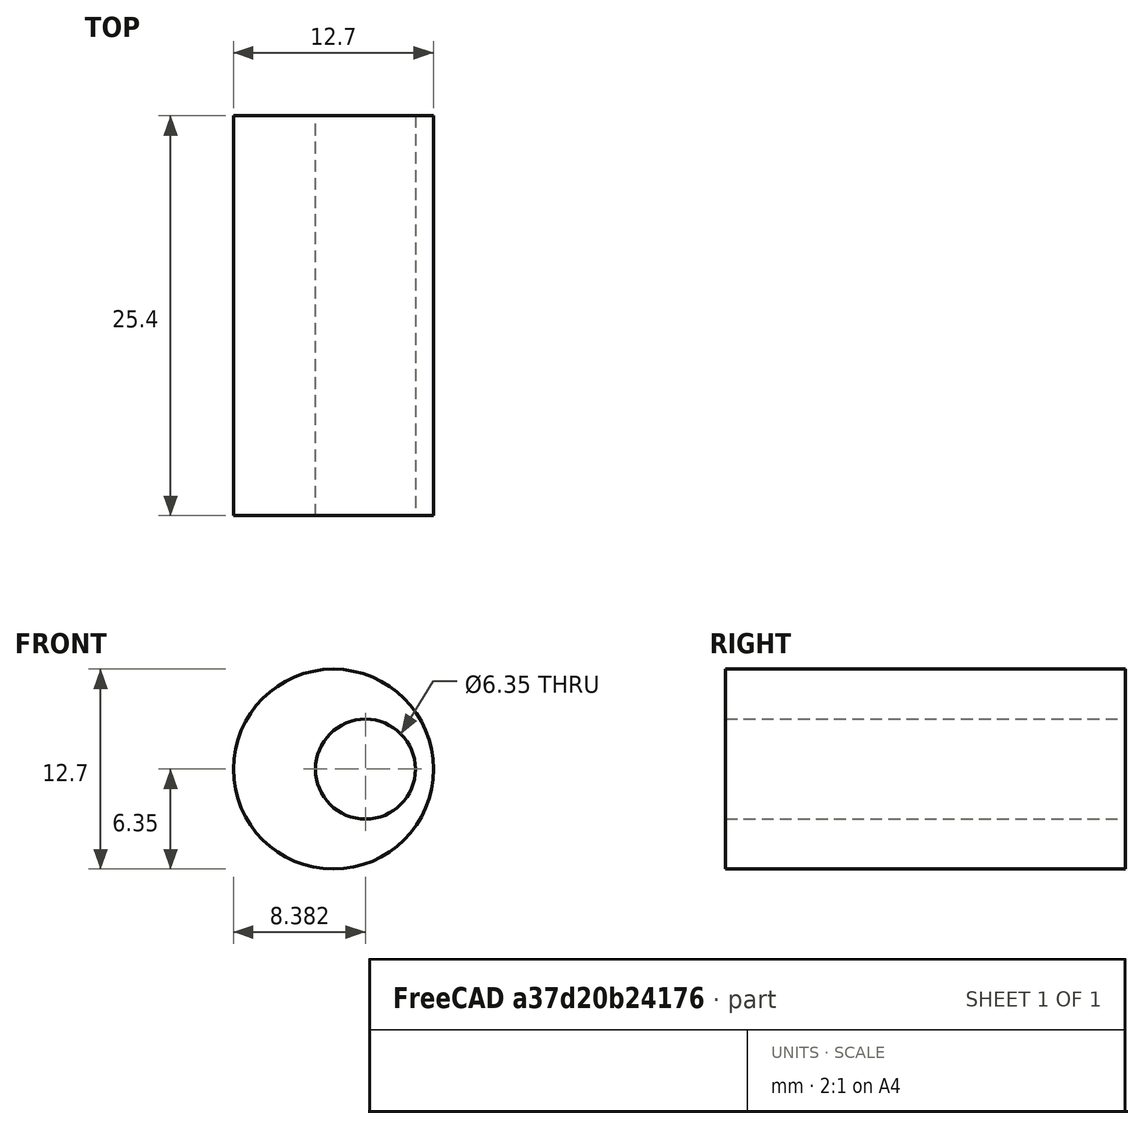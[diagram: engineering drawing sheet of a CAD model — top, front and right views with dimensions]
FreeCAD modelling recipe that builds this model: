
FCSTD DOCUMENT  (FreeCAD 0.21R31527 (Git))
Label: TempCam
License: All rights reserved
LicenseURL: http://en.wikipedia.org/wiki/All_rights_reserved
objects: Sketcher::SketchObject×1, PartDesign::Pad×1, PartDesign::Body×1
note: 4 computed .brp shape members not serialized (recipe doc carries the construction recipe); baked Part::Feature solids carry a one-line shape summary decoded from their .brp

FEATURE [Sketcher::SketchObject] Sketch
  FullyConstrained = true
  MapMode = 5
  Placement = pos=(0,0,0) rot=(1,0,0;1.5708rad)
  Support = -> [XZ_Plane]
  sketch-geometry (2):
    g0: Circle CenterX=0 CenterY=0 CenterZ=0 NormalX=0 NormalY=0 NormalZ=1 AngleXU=0 Radius=6.35
    g1: Circle CenterX=2.032 CenterY=0 CenterZ=0 NormalX=0 NormalY=0 NormalZ=1 AngleXU=0 Radius=3.175
  constraints (5):
    c: Coincident(g0,g-1)
    c: Diameter(g0) = 12.7
    c: PointOnObject(g1,g-1)
    c: Diameter(g1) = 6.35
    c: Distance(g1,g0) = 2.032
FEATURE [PartDesign::Pad] Pad
  Direction = (0,-1,2e-16)
  Length = 25.4
  Length2 = 10
  Placement = pos=(0,0,0) rot=(1,0,0;1.5708rad)
  Profile = -> Sketch
  ReferenceAxis = -> Sketch [N_Axis]
  Type = 0
FEATURE [PartDesign::Body] Body
  Group = -> [Sketch,Pad]
  Origin = -> Origin
  Tip = -> Pad
